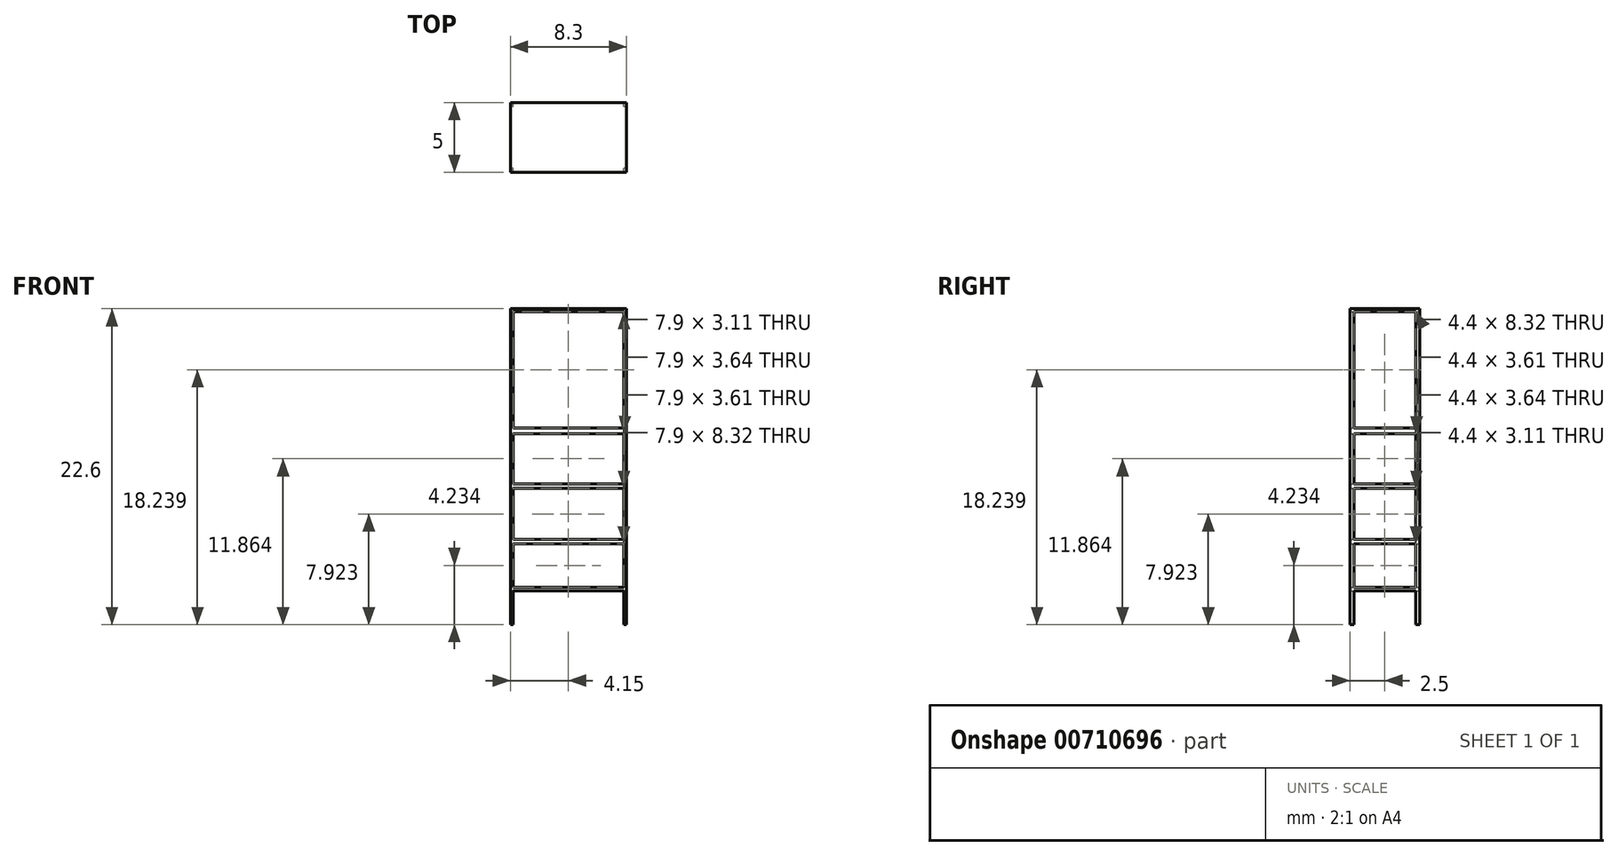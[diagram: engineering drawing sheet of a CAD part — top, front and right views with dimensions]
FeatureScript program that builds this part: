
annotation { "Feature Type Name" : "Feature", "Feature Type Description" : "" }
export const myFeature = defineFeature(function(context is Context, id is Id, definition is map)
    precondition{}
    {
        {
            var Q0;
            Q0=qCreatedBy(makeId("Top.planeOp"),FACE);
            var sketch = newSketch(context, id + "F0", { "sketchPlane" : qUnion([Q0])});
            skLineSegment(sketch, "E0.bottom", {"start": v(0, 0) * mm, "end": v(8.3, 0) * mm});
            skLineSegment(sketch, "E0.top", {"start": v(0, -5) * mm, "end": v(8.3, -5) * mm});
            skLineSegment(sketch, "E0.left", {"start": v(0, 0) * mm, "end": v(0, -5) * mm});
            skLineSegment(sketch, "E0.right", {"start": v(8.3, 0) * mm, "end": v(8.3, -5) * mm});
            skSolve(sketch);
        }
        {
            var Q0;
            Q0=qSketchRegion(id+"F0",true);
            extrude(context, id + "F1", {"entities" : qUnion([Q0]), "depth" : 22.6 * mm, "offsetDistance" : 25 * mm});
        }
        {
            var Q0;
            Q0=makeQuery(id+"F1.opExtrude","SWEPT_FACE",FACE,{"disambiguationData":[OSD([sQuery(id+"F0.wireOp",EDGE,"E0.bottom")])]});
            var sketch = newSketch(context, id + "F2", { "sketchPlane" : qUnion([Q0])});
            skLineSegment(sketch, "E1.0", {"start": v(-8.1, 0.2) * mm, "end": v(-0.2, 0.2) * mm, "construction": true});
            skLineSegment(sketch, "E1.1", {"start": v(-8.1, 22.4) * mm, "end": v(-8.1, 0.2) * mm, "construction": true});
            skLineSegment(sketch, "E1.2", {"start": v(-0.2, 22.4) * mm, "end": v(-8.1, 22.4) * mm, "construction": true});
            skLineSegment(sketch, "E1.3", {"start": v(-0.2, 0.2) * mm, "end": v(-0.2, 22.4) * mm, "construction": true});
            skLineSegment(sketch, "E2.bottom", {"start": v(-8.1, 22.4) * mm, "end": v(-0.2, 22.4) * mm, "construction": true});
            skLineSegment(sketch, "E2.top", {"start": v(-8.1, 14.08) * mm, "end": v(-0.2, 14.08) * mm, "construction": true});
            skLineSegment(sketch, "E2.left", {"start": v(-8.1, 22.4) * mm, "end": v(-8.1, 14.08) * mm, "construction": true});
            skLineSegment(sketch, "E2.right", {"start": v(-0.2, 22.4) * mm, "end": v(-0.2, 14.08) * mm, "construction": true});
            skLineSegment(sketch, "E3.bottom", {"start": v(-8.1, 22.4) * mm, "end": v(-0.2, 22.4) * mm});
            skLineSegment(sketch, "E3.top", {"start": v(-8.1, 14.08) * mm, "end": v(-0.2, 14.08) * mm});
            skLineSegment(sketch, "E3.left", {"start": v(-8.1, 22.4) * mm, "end": v(-8.1, 14.08) * mm});
            skLineSegment(sketch, "E3.right", {"start": v(-0.2, 22.4) * mm, "end": v(-0.2, 14.08) * mm});
            skLineSegment(sketch, "E4.bottom", {"start": v(-8.1, 13.67) * mm, "end": v(-0.2, 13.67) * mm});
            skLineSegment(sketch, "E4.top", {"start": v(-8.1, 10.06) * mm, "end": v(-0.2, 10.06) * mm});
            skLineSegment(sketch, "E4.left", {"start": v(-8.1, 13.67) * mm, "end": v(-8.1, 10.06) * mm});
            skLineSegment(sketch, "E4.right", {"start": v(-0.2, 13.67) * mm, "end": v(-0.2, 10.06) * mm});
            skLineSegment(sketch, "E5.bottom", {"start": v(-8.1, 9.74) * mm, "end": v(-0.2, 9.74) * mm});
            skLineSegment(sketch, "E5.top", {"start": v(-8.1, 6.1) * mm, "end": v(-0.2, 6.1) * mm});
            skLineSegment(sketch, "E5.left", {"start": v(-8.1, 9.74) * mm, "end": v(-8.1, 6.1) * mm});
            skLineSegment(sketch, "E5.right", {"start": v(-0.2, 9.74) * mm, "end": v(-0.2, 6.1) * mm});
            skLineSegment(sketch, "E6.bottom", {"start": v(-8.1, 5.79) * mm, "end": v(-0.2, 5.79) * mm});
            skLineSegment(sketch, "E6.top", {"start": v(-8.1, 2.68) * mm, "end": v(-0.2, 2.68) * mm});
            skLineSegment(sketch, "E6.left", {"start": v(-8.1, 5.79) * mm, "end": v(-8.1, 2.68) * mm});
            skLineSegment(sketch, "E6.right", {"start": v(-0.2, 5.79) * mm, "end": v(-0.2, 2.68) * mm});
            skLineSegment(sketch, "E7.bottom", {"start": v(-8.1, 2.43) * mm, "end": v(-0.2, 2.43) * mm});
            skLineSegment(sketch, "E7.top", {"start": v(-8.1, 0) * mm, "end": v(-0.2, 0) * mm});
            skLineSegment(sketch, "E7.left", {"start": v(-8.1, 2.43) * mm, "end": v(-8.1, 0) * mm});
            skLineSegment(sketch, "E7.right", {"start": v(-0.2, 2.43) * mm, "end": v(-0.2, 0) * mm});
            skSolve(sketch);
        }
        {
            var Q0;
            Q0=makeQuery(id+"F2.imprint","IMPRINT",FACE,{"disambiguationData":[TD([[makeQuery(id+"F2.imprint","IMPRINT",EDGE,{"derivedFrom":sQuery(id+"F2.wireOp",EDGE,"E3.bottom")}),-1.0]])]});
            var Q1;
            Q1=makeQuery(id+"F2.imprint","IMPRINT",FACE,{"disambiguationData":[TD([[makeQuery(id+"F2.imprint","IMPRINT",EDGE,{"derivedFrom":sQuery(id+"F2.wireOp",EDGE,"E4.bottom")}),-1.0]])]});
            var Q2;
            Q2=makeQuery(id+"F2.imprint","IMPRINT",FACE,{"disambiguationData":[TD([[makeQuery(id+"F2.imprint","IMPRINT",EDGE,{"derivedFrom":sQuery(id+"F2.wireOp",EDGE,"E5.bottom")}),-1.0]])]});
            var Q3;
            Q3=makeQuery(id+"F2.imprint","IMPRINT",FACE,{"disambiguationData":[TD([[makeQuery(id+"F2.imprint","IMPRINT",EDGE,{"derivedFrom":sQuery(id+"F2.wireOp",EDGE,"E6.bottom")}),-1.0]])]});
            var Q4;
            Q4=makeQuery(id+"F2.imprint","IMPRINT",FACE,{"disambiguationData":[TD([[makeQuery(id+"F2.imprint","IMPRINT",EDGE,{"derivedFrom":sQuery(id+"F2.wireOp",EDGE,"E7.bottom")}),-1.0]])]});
            extrude(context, id + "F3", {"entities" : qUnion([Q0, Q1, Q2, Q3, Q4]), "operationType" : NewBodyOperationType.REMOVE, "oppositeDirection" : true, "depth" : 25 * mm, "offsetDistance" : 25 * mm});
        }
        {
            var Q0;
            Q0=qCreatedBy(makeId("Right.planeOp"),FACE);
            var sketch = newSketch(context, id + "F4", { "sketchPlane" : qUnion([Q0])});
            skLineSegment(sketch, "E8.0", {"start": v(-4.7, 17.9) * mm, "end": v(-4.7, 0) * mm, "construction": true});
            skLineSegment(sketch, "E9.0", {"start": v(-0.3, 17.9) * mm, "end": v(-0.3, 0) * mm, "construction": true});
            skLineSegment(sketch, "E10.0", {"start": v(-5, 22.4) * mm, "end": v(0, 22.4) * mm});
            skLineSegment(sketch, "E11.0", {"start": v(-5, 14.08) * mm, "end": v(0, 14.08) * mm});
            skPoint(sketch, "E12.0", {"position": v(-2.5, 13.67) * mm});
            skLineSegment(sketch, "E13.0", {"start": v(-5, 13.67) * mm, "end": v(0, 13.67) * mm});
            skLineSegment(sketch, "E14.0", {"start": v(-5, 10.06) * mm, "end": v(0, 10.06) * mm});
            skLineSegment(sketch, "E15.0", {"start": v(-5, 9.74) * mm, "end": v(0, 9.74) * mm});
            skLineSegment(sketch, "E16.bottom", {"start": v(-4.7, 22.4) * mm, "end": v(-0.3, 22.4) * mm});
            skLineSegment(sketch, "E16.top", {"start": v(-4.7, 14.08) * mm, "end": v(-0.3, 14.08) * mm});
            skLineSegment(sketch, "E16.left", {"start": v(-4.7, 22.4) * mm, "end": v(-4.7, 14.08) * mm});
            skLineSegment(sketch, "E16.right", {"start": v(-0.3, 22.4) * mm, "end": v(-0.3, 14.08) * mm});
            skLineSegment(sketch, "E17.bottom", {"start": v(-4.7, 13.67) * mm, "end": v(-0.3, 13.67) * mm});
            skLineSegment(sketch, "E17.top", {"start": v(-4.7, 10.06) * mm, "end": v(-0.3, 10.06) * mm});
            skLineSegment(sketch, "E17.left", {"start": v(-4.7, 13.67) * mm, "end": v(-4.7, 10.06) * mm});
            skLineSegment(sketch, "E17.right", {"start": v(-0.3, 13.67) * mm, "end": v(-0.3, 10.06) * mm});
            skLineSegment(sketch, "E18.0", {"start": v(-5, 6.1) * mm, "end": v(0, 6.1) * mm});
            skLineSegment(sketch, "E19.0", {"start": v(-5, 5.79) * mm, "end": v(0, 5.79) * mm});
            skLineSegment(sketch, "E20.0", {"start": v(-5, 2.68) * mm, "end": v(0, 2.68) * mm});
            skLineSegment(sketch, "E21.0", {"start": v(-5, 2.43) * mm, "end": v(0, 2.43) * mm});
            skLineSegment(sketch, "E22.bottom", {"start": v(-4.7, 9.74) * mm, "end": v(-0.3, 9.74) * mm});
            skLineSegment(sketch, "E22.top", {"start": v(-4.7, 6.1) * mm, "end": v(-0.3, 6.1) * mm});
            skLineSegment(sketch, "E22.left", {"start": v(-4.7, 9.74) * mm, "end": v(-4.7, 6.1) * mm});
            skLineSegment(sketch, "E22.right", {"start": v(-0.3, 9.74) * mm, "end": v(-0.3, 6.1) * mm});
            skLineSegment(sketch, "E23.bottom", {"start": v(-4.7, 5.79) * mm, "end": v(-0.3, 5.79) * mm});
            skLineSegment(sketch, "E23.top", {"start": v(-4.7, 2.68) * mm, "end": v(-0.3, 2.68) * mm});
            skLineSegment(sketch, "E23.left", {"start": v(-4.7, 5.79) * mm, "end": v(-4.7, 2.68) * mm});
            skLineSegment(sketch, "E23.right", {"start": v(-0.3, 5.79) * mm, "end": v(-0.3, 2.68) * mm});
            skLineSegment(sketch, "E24.bottom", {"start": v(-4.7, 2.43) * mm, "end": v(-0.3, 2.43) * mm});
            skLineSegment(sketch, "E24.top", {"start": v(-4.7, 0) * mm, "end": v(-0.3, 0) * mm});
            skLineSegment(sketch, "E24.left", {"start": v(-4.7, 2.43) * mm, "end": v(-4.7, 0) * mm});
            skLineSegment(sketch, "E24.right", {"start": v(-0.3, 2.43) * mm, "end": v(-0.3, 0) * mm});
            skSolve(sketch);
        }
        {
            var Q0;
            Q0=qSketchRegion(id+"F4",true);
            extrude(context, id + "F5", {"entities" : qUnion([Q0]), "operationType" : NewBodyOperationType.REMOVE, "depth" : 25 * mm, "offsetDistance" : 25 * mm});
        }
    });
